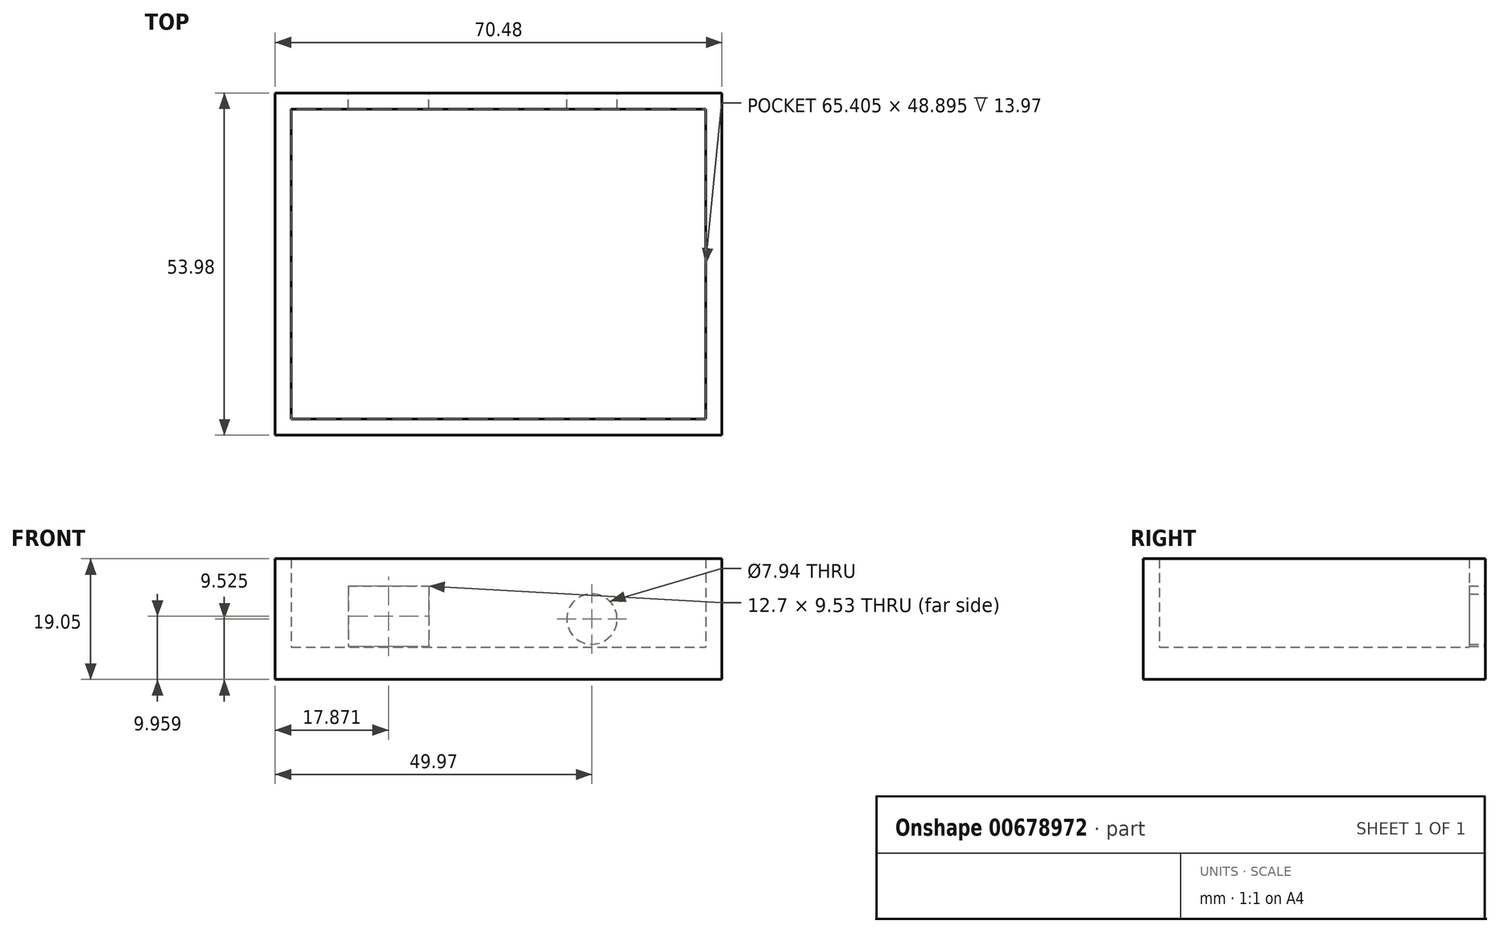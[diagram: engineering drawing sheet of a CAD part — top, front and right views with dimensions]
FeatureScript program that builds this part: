
annotation { "Feature Type Name" : "Feature", "Feature Type Description" : "" }
export const myFeature = defineFeature(function(context is Context, id is Id, definition is map)
    precondition{}
    {
        {
            var Q0;
            Q0=qCreatedBy(makeId("Top.planeOp"),FACE);
            var sketch = newSketch(context, id + "F0", { "sketchPlane" : qUnion([Q0])});
            skLineSegment(sketch, "E0.bottom", {"start": v(-35.24, -26.99) * mm, "end": v(35.24, -26.99) * mm});
            skLineSegment(sketch, "E0.top", {"start": v(-35.24, 26.99) * mm, "end": v(35.24, 26.99) * mm});
            skLineSegment(sketch, "E0.left", {"start": v(-35.24, -26.99) * mm, "end": v(-35.24, 26.99) * mm});
            skLineSegment(sketch, "E0.right", {"start": v(35.24, -26.99) * mm, "end": v(35.24, 26.99) * mm});
            skPoint(sketch, "E0.middle", {"position": v(0, 0) * mm});
            skSolve(sketch);
        }
        {
            var Q0;
            Q0=qSketchRegion(id+"F0",true);
            extrude(context, id + "F1", {"entities" : qUnion([Q0]), "depth" : 19.05 * mm, "offsetDistance" : 25.4 * mm});
        }
        {
            var Q0;
            Q0=makeQuery(id+"F1.opExtrude","CAP_FACE",FACE,{"disambiguationData":[OSD([sQuery(id+"F0.wireOp",EDGE,"E0.bottom"),sQuery(id+"F0.wireOp",EDGE,"E0.top"),sQuery(id+"F0.wireOp",EDGE,"E0.left"),sQuery(id+"F0.wireOp",EDGE,"E0.right")])],"isStart":false});
            shell(context, id + "F2", {"entities" : qUnion([Q0]), "thickness" : 2.54 * mm});
        }
        {
            var Q0;
            Q0=makeQuery(id+"F1.opExtrude","SWEPT_FACE",FACE,{"disambiguationData":[OSD([sQuery(id+"F0.wireOp",EDGE,"E0.top")])]});
            var sketch = newSketch(context, id + "F3", { "sketchPlane" : qUnion([Q0])});
            skLineSegment(sketch, "E1.bottom", {"start": v(23.72, 14.72) * mm, "end": v(11.02, 14.72) * mm});
            skLineSegment(sketch, "E1.top", {"start": v(23.72, 5.2) * mm, "end": v(11.02, 5.2) * mm});
            skLineSegment(sketch, "E1.left", {"start": v(23.72, 14.72) * mm, "end": v(23.72, 5.2) * mm});
            skLineSegment(sketch, "E1.right", {"start": v(11.02, 14.72) * mm, "end": v(11.02, 5.2) * mm});
            skPoint(sketch, "E1.middle", {"position": v(17.37, 9.96) * mm});
            skSolve(sketch);
        }
        {
            var Q0;
            Q0=qSketchRegion(id+"F3",true);
            extrude(context, id + "F4", {"entities" : qUnion([Q0]), "operationType" : NewBodyOperationType.REMOVE, "oppositeDirection" : true, "depth" : 3.3 * mm, "offsetDistance" : 25.4 * mm});
        }
        {
            var Q0;
            Q0=makeQuery(id+"F1.opExtrude","SWEPT_FACE",FACE,{"disambiguationData":[OSD([sQuery(id+"F0.wireOp",EDGE,"E0.top")])]});
            var sketch = newSketch(context, id + "F5", { "sketchPlane" : qUnion([Q0])});
            skLineSegment(sketch, "E2", {"start": v(-35.24, 9.53) * mm, "end": v(-14.73, 9.53) * mm});
            skSolve(sketch);
        }
        {
            var Q0;
            Q0=sQuery(id+"F5.wireOp",VERTEX,"E2.end");
            var Q1;
            Q1=makeQuery(id+"F1.opExtrude","SWEPT_BODY",BODY,{"disambiguationData":[OSD([sQuery(id+"F0.wireOp",EDGE,"E0.bottom"),sQuery(id+"F0.wireOp",EDGE,"E0.top"),sQuery(id+"F0.wireOp",EDGE,"E0.left"),sQuery(id+"F0.wireOp",EDGE,"E0.right")])]});
            hole(context, id + "F6", {"style" : HoleStyle.SIMPLE, "endStyle" : HoleEndStyle.BLIND, "holeDiameter" : 7.94 * mm, "majorDiameter" : 6.35 * mm, "holeDepth" : 12.7 * mm, "isTappedThrough" : true, "tappedDepth" : 12.7 * mm, "tapClearance" : 3, "locations" : qUnion([Q0]), "scope" : qUnion([Q1])});
        }
        {
            var Q0;
            Q0=makeQuery(id+"F2.opShell","OFFSET_FACE",FACE,{"disambiguationData":[OSD([sQuery(id+"F0.wireOp",EDGE,"E0.bottom"),sQuery(id+"F0.wireOp",EDGE,"E0.top"),sQuery(id+"F0.wireOp",EDGE,"E0.left"),sQuery(id+"F0.wireOp",EDGE,"E0.right")])]});
            extrude(context, id + "F7", {"entities" : qUnion([Q0]), "operationType" : NewBodyOperationType.ADD, "depth" : 2.54 * mm, "offsetDistance" : 25.4 * mm});
        }
    });
